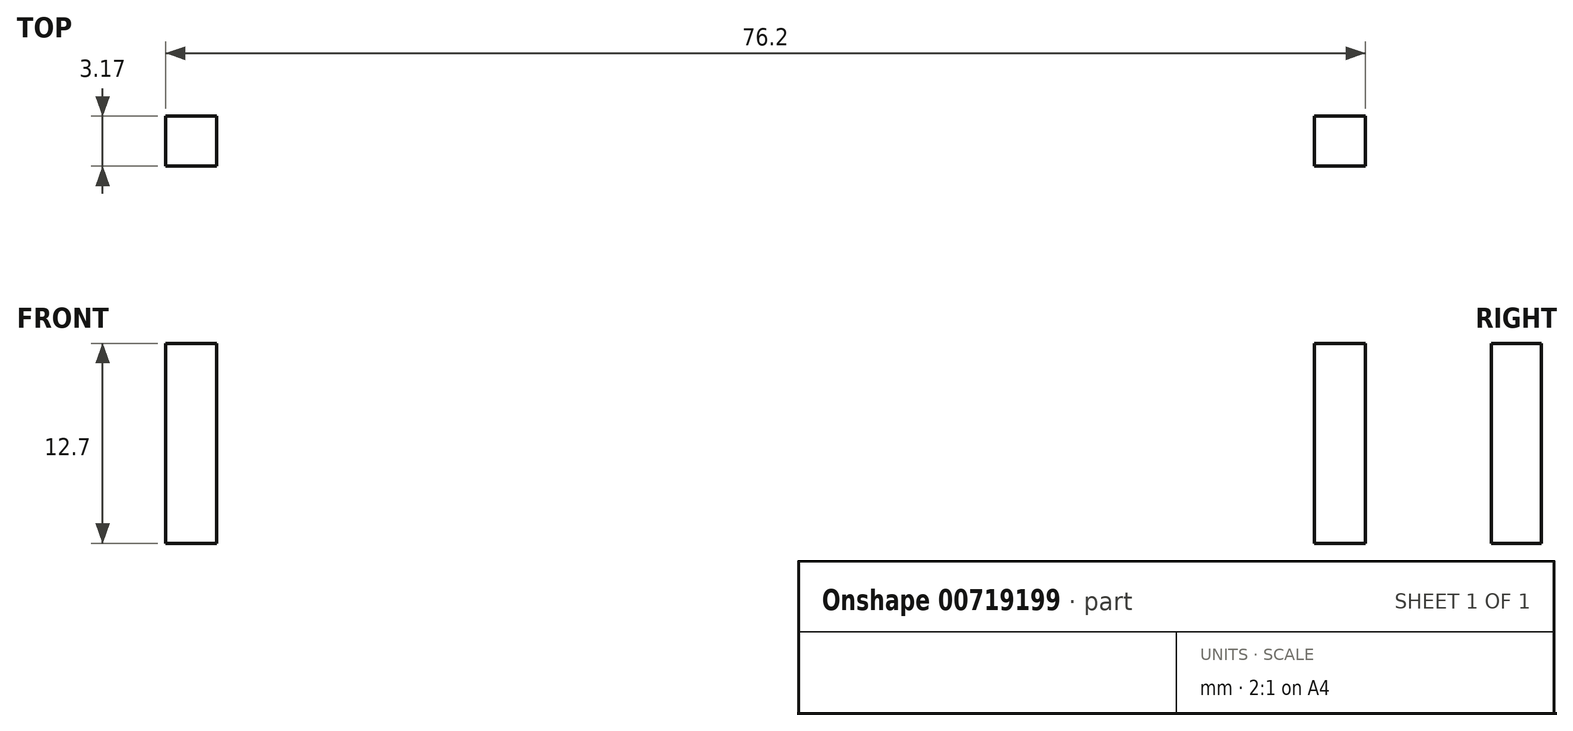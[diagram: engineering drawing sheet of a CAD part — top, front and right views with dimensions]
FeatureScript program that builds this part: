
annotation { "Feature Type Name" : "Feature", "Feature Type Description" : "" }
export const myFeature = defineFeature(function(context is Context, id is Id, definition is map)
    precondition{}
    {
        {
            var Q0;
            Q0=qCreatedBy(makeId("Front.planeOp"),FACE);
            var sketch = newSketch(context, id + "F0", { "sketchPlane" : qUnion([Q0])});
            skLineSegment(sketch, "E0.bottom", {"start": v(38.1, 19.05) * mm, "end": v(-38.1, 19.05) * mm});
            skLineSegment(sketch, "E0.top", {"start": v(38.1, -19.05) * mm, "end": v(-38.1, -19.05) * mm});
            skPoint(sketch, "E0.middle", {"position": v(0, 0) * mm});
            skLineSegment(sketch, "E1.bottom", {"start": v(-38.1, 19.05) * mm, "end": v(-34.87, 19.05) * mm});
            skLineSegment(sketch, "E1.top", {"start": v(-38.1, 6.35) * mm, "end": v(-34.87, 6.35) * mm});
            skLineSegment(sketch, "E1.left", {"start": v(-38.1, 19.05) * mm, "end": v(-38.1, 6.35) * mm});
            skLineSegment(sketch, "E1.right", {"start": v(-34.87, 19.05) * mm, "end": v(-34.87, 6.35) * mm});
            skLineSegment(sketch, "E2.bottom", {"start": v(-38.1, -19.05) * mm, "end": v(-34.87, -19.05) * mm});
            skLineSegment(sketch, "E2.top", {"start": v(-38.1, -6.35) * mm, "end": v(-34.87, -6.35) * mm});
            skLineSegment(sketch, "E2.left", {"start": v(-38.1, -19.05) * mm, "end": v(-38.1, -6.35) * mm});
            skLineSegment(sketch, "E2.right", {"start": v(-34.87, -19.05) * mm, "end": v(-34.87, -6.35) * mm});
            skLineSegment(sketch, "E3.bottom", {"start": v(38.1, -19.05) * mm, "end": v(34.87, -19.05) * mm});
            skLineSegment(sketch, "E3.top", {"start": v(38.1, -6.35) * mm, "end": v(34.87, -6.35) * mm});
            skLineSegment(sketch, "E3.left", {"start": v(38.1, -19.05) * mm, "end": v(38.1, -6.35) * mm});
            skLineSegment(sketch, "E3.right", {"start": v(34.87, -19.05) * mm, "end": v(34.87, -6.35) * mm});
            skLineSegment(sketch, "E4.bottom", {"start": v(38.1, 19.05) * mm, "end": v(34.87, 19.05) * mm});
            skLineSegment(sketch, "E4.top", {"start": v(38.1, 6.35) * mm, "end": v(34.87, 6.35) * mm});
            skLineSegment(sketch, "E4.left", {"start": v(38.1, 19.05) * mm, "end": v(38.1, 6.35) * mm});
            skLineSegment(sketch, "E4.right", {"start": v(34.87, 19.05) * mm, "end": v(34.87, 6.35) * mm});
            skLineSegment(sketch, "E5", {"start": v(38.1, 6.35) * mm, "end": v(38.1, -6.35) * mm, "construction": true});
            skLineSegment(sketch, "E6", {"start": v(-38.1, 6.35) * mm, "end": v(-38.1, -6.35) * mm, "construction": true});
            skLineSegment(sketch, "E7", {"start": v(-38.1, 6.35) * mm, "end": v(-38.1, -6.35) * mm});
            skLineSegment(sketch, "E8", {"start": v(38.1, 6.35) * mm, "end": v(38.1, -6.35) * mm});
            skSolve(sketch);
        }
        {
            var Q0;
            Q0=makeQuery(id+"F0.imprint","IMPRINT",FACE,{"disambiguationData":[TD([[makeQuery(id+"F0.imprint","IMPRINT",EDGE,{"derivedFrom":sQuery(id+"F0.wireOp",EDGE,"E0.bottom")}),1.0]])]});
            extrude(context, id + "F1", {"entities" : qUnion([Q0]), "depth" : 3.17 * mm, "offsetDistance" : 25.4 * mm});
        }
    });
